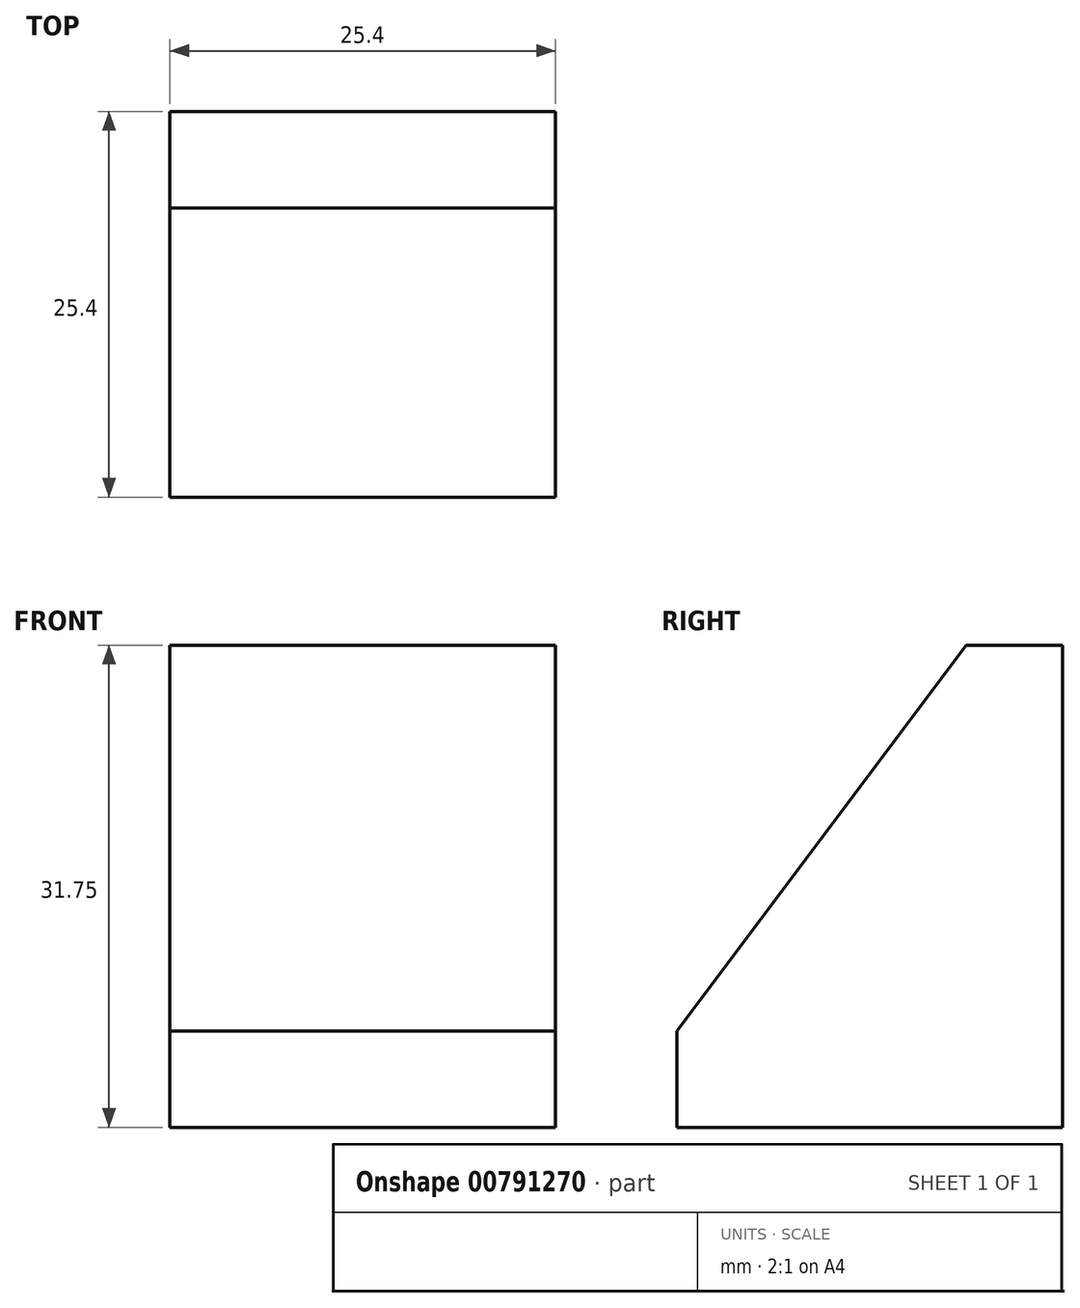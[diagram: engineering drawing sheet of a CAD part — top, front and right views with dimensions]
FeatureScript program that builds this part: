
annotation { "Feature Type Name" : "Feature", "Feature Type Description" : "" }
export const myFeature = defineFeature(function(context is Context, id is Id, definition is map)
    precondition{}
    {
        {
            var Q0;
            Q0=qCreatedBy(makeId("Right.planeOp"),FACE);
            var sketch = newSketch(context, id + "F0", { "sketchPlane" : qUnion([Q0])});
            skLineSegment(sketch, "E0", {"start": v(0, 0) * mm, "end": v(25.4, 0) * mm});
            skLineSegment(sketch, "E1", {"start": v(25.4, 0) * mm, "end": v(25.4, 31.75) * mm});
            skLineSegment(sketch, "E2", {"start": v(25.4, 31.75) * mm, "end": v(19.05, 31.75) * mm});
            skLineSegment(sketch, "E3", {"start": v(0, 0) * mm, "end": v(0, 6.35) * mm});
            skLineSegment(sketch, "E4", {"start": v(19.05, 31.75) * mm, "end": v(0, 6.35) * mm});
            skSolve(sketch);
        }
        {
            var Q0;
            Q0=makeQuery(id+"F0.imprint","IMPRINT",FACE,{"disambiguationData":[TD([[makeQuery(id+"F0.imprint","IMPRINT",EDGE,{"derivedFrom":sQuery(id+"F0.wireOp",EDGE,"E0")}),1.0]])]});
            extrude(context, id + "F1", {"entities" : qUnion([Q0]), "depth" : 25.4 * mm, "offsetDistance" : 25.4 * mm});
        }
    });
